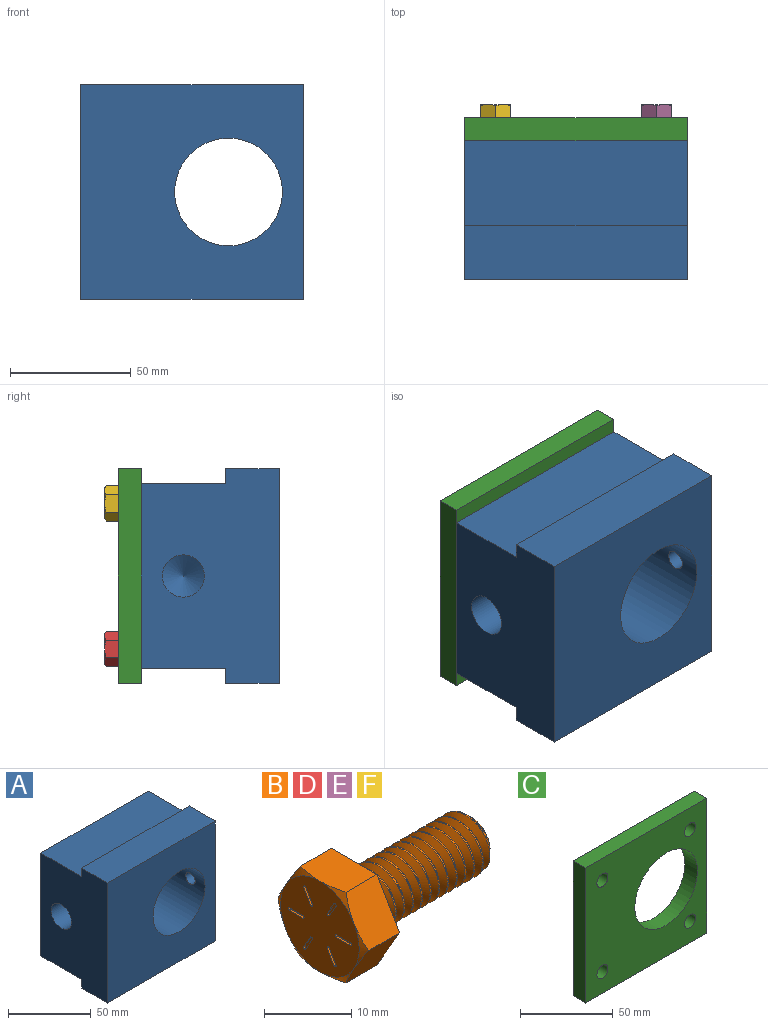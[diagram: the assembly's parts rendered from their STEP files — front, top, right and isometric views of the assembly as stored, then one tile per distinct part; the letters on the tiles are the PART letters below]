
ASSEMBLY  parts=6 mates=5
PART A: 22 faces, bbox 92.1x57.2x88.9 mm
  f0: cylinder r=22.29mm len=57.15mm, axis (0,1,0), area 7953.9mm2, adj f1,f6,f11
  f1: plane 92.08x76.2mm, normal (0,1,0), area 5321.6mm2, adj f0,f2,f4,f7,f9,f15,f17,f19
  f2: plane 88.9x57.15mm, normal (1,0,0), area 4587.6mm2, adj f1,f3,f5,f6,f7,f8,f9,f10
  f3: plane 92.08x22.23mm, normal (0,0,1), area 2046.4mm2, adj f2,f4,f6,f10
  f4: plane 88.9x57.15mm, normal (-1,0,0), area 4397.6mm2, adj f1,f3,f5,f6,f7,f8,f9,f10
  f5: plane 92.08x22.23mm, normal (0,0,-1), area 2046.4mm2, adj f2,f4,f6,f8
  f6: plane 92.08x88.9mm, normal (0,-1,0), area 6624.8mm2, adj f0,f2,f3,f4,f5
  f7: plane 92.08x34.93mm, normal (0,0,-1), area 3215.7mm2, adj f1,f2,f4,f8
  f8: plane 92.08x6.35mm, normal (0,1,0), area 584.7mm2, adj f2,f4,f5,f7
  f9: plane 92.08x34.93mm, normal (0,0,1), area 3215.7mm2, adj f1,f2,f4,f10
  f10: plane 92.08x6.35mm, normal (0,1,0), area 584.7mm2, adj f2,f3,f4,f9
  f11: cylinder r=3.97mm len=8.99mm, axis (1,0,0), area 219.8mm2, adj f0,f2
  f12: cone r=0mm half-angle=59deg, axis (-1,0,0), area 279.4mm2, adj f13
  f13: cylinder r=8.73mm len=33.34mm, axis (-1,0,0), area 1828.9mm2, adj f4,f12
  f14: cone r=0mm half-angle=59deg, axis (0,1,0), area 39mm2, adj f15
  f15: cylinder r=3.26mm len=25.4mm, axis (0,1,0), area 520.9mm2, adj f1,f14
  f16: cone r=0mm half-angle=59deg, axis (0,1,0), area 39mm2, adj f17
  f17: cylinder r=3.26mm len=25.4mm, axis (0,1,0), area 520.9mm2, adj f1,f16
  f18: cone r=0mm half-angle=59deg, axis (0,1,0), area 39mm2, adj f19
  f19: cylinder r=3.26mm len=25.4mm, axis (0,1,0), area 520.9mm2, adj f1,f18
  f20: cone r=0mm half-angle=59deg, axis (0,1,0), area 39mm2, adj f21
  f21: cylinder r=3.26mm len=25.4mm, axis (0,1,0), area 520.9mm2, adj f1,f20
PART B: 50 faces, bbox 25.7x15.3x15.3 mm
  f0: cylinder r=0.19mm len=0.36mm, axis (-1,0,0), area 0.2mm2, adj f23,f47,f48,f49
  f1: cylinder r=0.19mm len=0.36mm, axis (-1,0,0), area 0.2mm2, adj f23,f43,f44,f45
  f2: cylinder r=0.19mm len=0.36mm, axis (-1,0,0), area 0.2mm2, adj f23,f33,f35,f36
  f3: cylinder r=0.19mm len=0.36mm, axis (-1,0,0), area 0.2mm2, adj f23,f29,f31,f32
  f4: cone r=2.91mm half-angle=45deg, axis (-1,0,0), area 17.6mm2, adj f5,f12,f13,f14,f15
  f5: cylinder r=3.97mm len=17.99mm, axis (1,0,0), area 56.1mm2, adj f4,f14,f15,f16
  f6: plane 7.94x6.16mm, normal (0,0,1), area 39.3mm2, adj f7,f11,f16,f17,f22
  f7: plane 6.95x6.16mm, normal (0,0.87,0.5), area 39.3mm2, adj f6,f8,f16,f21,f22
  f8: plane 6.95x6.16mm, normal (0,0.87,-0.5), area 39.3mm2, adj f7,f9,f16,f20,f21
  f9: plane 7.94x6.16mm, normal (0,0,-1), area 39.3mm2, adj f8,f10,f16,f19,f20
  f10: plane 6.95x6.16mm, normal (0,-0.87,-0.5), area 39.3mm2, adj f9,f11,f16,f18,f19
  f11: plane 6.95x6.16mm, normal (0,-0.87,0.5), area 39.3mm2, adj f6,f10,f16,f17,f18
  f12: plane 5.82x5.82mm, normal (1,0,0), area 26.6mm2, adj f4
  f13: cylinder r=3.05mm len=18.91mm, axis (1,0,0), area 45.5mm2, adj f4,f14,f15,f16
  f14: bspline ~19.58x7.94mm, area 305.8mm2, adj f4,f5,f13,f16
  f15: bspline ~20.11x7.94mm, area 307.1mm2, adj f4,f5,f13,f16
  f16: plane 15.21x13.24mm, normal (1,0,0), area 100.6mm2, adj f5,f6,f7,f8,f9,f10,f11,f13
  f17: cone r=6.35mm half-angle=60deg, axis (1,0,0), area 4mm2, adj f6,f11,f23
  f18: cone r=6.35mm half-angle=60deg, axis (1,0,0), area 4mm2, adj f10,f11,f23
  f19: cone r=6.35mm half-angle=60deg, axis (1,0,0), area 4mm2, adj f9,f10,f23
  f20: cone r=6.35mm half-angle=60deg, axis (1,0,0), area 4mm2, adj f8,f9,f23
  f21: cone r=6.35mm half-angle=60deg, axis (1,0,0), area 4mm2, adj f7,f8,f23
  f22: cone r=6.35mm half-angle=60deg, axis (1,0,0), area 4mm2, adj f6,f7,f23
  f23: plane 12.7x12.7mm, normal (-1,0,0), area 121.1mm2, adj f0,f1,f2,f3,f17,f18,f19,f20
  f24: cylinder r=0.19mm len=0.38mm, axis (-1,0,0), area 0.2mm2, adj f23,f25,f27,f28
  f25: plane 2.16x0.25mm, normal (0,0,-1), area 0.5mm2, adj f23,f24,f26,f28
  f26: cylinder r=0.19mm len=0.38mm, axis (-1,0,0), area 0.2mm2, adj f23,f25,f27,f28
  f27: plane 2.16x0.25mm, normal (0,0,1), area 0.5mm2, adj f23,f24,f26,f28
  f28: plane 2.54x0.38mm, normal (-1,0,0), area 0.9mm2, adj f24,f25,f26,f27
  f29: plane 1.87x1.08mm, normal (0,0.87,-0.5), area 0.5mm2, adj f3,f23,f30,f32
  f30: cylinder r=0.19mm len=0.36mm, axis (-1,0,0), area 0.2mm2, adj f23,f29,f31,f32
  f31: plane 1.87x1.08mm, normal (0,-0.87,0.5), area 0.5mm2, adj f3,f23,f30,f32
  f32: plane 2.25x1.46mm, normal (-1,0,0), area 0.9mm2, adj f3,f29,f30,f31
  f33: plane 1.87x1.08mm, normal (0,0.87,0.5), area 0.5mm2, adj f2,f23,f34,f36
  f34: cylinder r=0.19mm len=0.36mm, axis (-1,0,0), area 0.2mm2, adj f23,f33,f35,f36
  f35: plane 1.87x1.08mm, normal (0,-0.87,-0.5), area 0.5mm2, adj f2,f23,f34,f36
  f36: plane 2.25x1.46mm, normal (-1,0,0), area 0.9mm2, adj f2,f33,f34,f35
  f37: cylinder r=0.19mm len=0.38mm, axis (-1,0,0), area 0.2mm2, adj f23,f38,f40,f41
  f38: plane 2.16x0.25mm, normal (0,0,1), area 0.5mm2, adj f23,f37,f39,f41
  f39: cylinder r=0.19mm len=0.38mm, axis (-1,0,0), area 0.2mm2, adj f23,f38,f40,f41
  f40: plane 2.16x0.25mm, normal (0,0,-1), area 0.5mm2, adj f23,f37,f39,f41
  f41: plane 2.54x0.38mm, normal (-1,0,0), area 0.9mm2, adj f37,f38,f39,f40
  f42: cylinder r=0.19mm len=0.36mm, axis (-1,0,0), area 0.2mm2, adj f23,f43,f44,f45
  f43: plane 1.87x1.08mm, normal (0,-0.87,0.5), area 0.5mm2, adj f1,f23,f42,f45
  f44: plane 1.87x1.08mm, normal (0,0.87,-0.5), area 0.5mm2, adj f1,f23,f42,f45
  f45: plane 2.25x1.46mm, normal (-1,0,0), area 0.9mm2, adj f1,f42,f43,f44
  f46: cylinder r=0.19mm len=0.36mm, axis (-1,0,0), area 0.2mm2, adj f23,f47,f48,f49
  f47: plane 1.87x1.08mm, normal (0,-0.87,-0.5), area 0.5mm2, adj f0,f23,f46,f49
  f48: plane 1.87x1.08mm, normal (0,0.87,0.5), area 0.5mm2, adj f0,f23,f46,f49
  f49: plane 2.25x1.46mm, normal (-1,0,0), area 0.9mm2, adj f0,f46,f47,f48
PART C: 11 faces, bbox 92.1x9.5x88.9 mm
  f0: plane 88.9x9.53mm, normal (1,0,0), area 846.8mm2, adj f1,f4,f5,f6
  f1: plane 92.08x9.53mm, normal (0,0,1), area 877mm2, adj f0,f2,f5,f6
  f2: plane 88.9x9.53mm, normal (-1,0,0), area 846.8mm2, adj f1,f4,f5,f6
  f3: cylinder r=23.81mm len=47.63mm, axis (0,1,0), area 1425.1mm2, adj f5,f6
  f4: plane 92.08x9.53mm, normal (0,0,-1), area 877mm2, adj f0,f2,f5,f6
  f5: plane 92.08x88.9mm, normal (0,-1,0), area 6180.7mm2, adj f0,f1,f2,f3,f4,f7,f8,f9
  f6: plane 92.08x88.9mm, normal (0,1,0), area 6180.7mm2, adj f0,f1,f2,f3,f4,f7,f8,f9
  f7: cylinder r=4.22mm len=9.53mm, axis (0,1,0), area 252.3mm2, adj f5,f6
  f8: cylinder r=4.22mm len=9.53mm, axis (0,1,0), area 252.3mm2, adj f5,f6
  f9: cylinder r=4.22mm len=9.53mm, axis (0,1,0), area 252.3mm2, adj f5,f6
  f10: cylinder r=4.22mm len=9.53mm, axis (0,1,0), area 252.3mm2, adj f5,f6
PART D: same geometry as B
PART E: same geometry as B
PART F: same geometry as B
PLACE A t=(-48.03,40.51,-24.81)mm
PLACE B rot(axis=(0.58,-0.58,-0.58),120deg) t=(31.34,43.29,-10.52)mm
PLACE C t=(-48.03,50.04,-24.81)mm
PLACE D rot(axis=(0.58,-0.58,-0.58),120deg) t=(-35.33,43.29,-10.52)mm
PLACE E rot(axis=(0.58,-0.58,-0.58),120deg) t=(31.34,43.29,49.8)mm
PLACE F rot(axis=(0.58,-0.58,-0.58),120deg) t=(-35.27,43.29,49.64)mm
MATE fastened D.f4 <-> C.f9  axis (0,-1,0) through (-35.33,50.04,-10.52)mm
MATE fastened F.f16 <-> C.f10  axis (0,-1,0) through (-35.33,50.04,49.8)mm
MATE fastened E.f4 <-> C.f7  axis (0,-1,0) through (31.34,50.04,49.8)mm
MATE fastened C.f3 <-> A.f0  axis (0,-1,0) through (13.12,40.51,19.64)mm
MATE fastened B.f4 <-> C.f8  axis (0,-1,0) through (31.34,50.04,-10.52)mm
